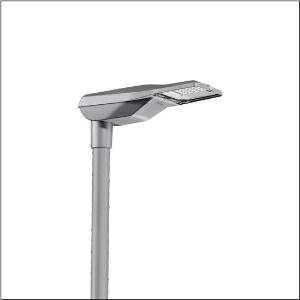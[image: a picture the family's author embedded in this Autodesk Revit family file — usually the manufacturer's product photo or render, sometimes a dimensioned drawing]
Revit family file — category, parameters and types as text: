
# Revit family: streetlight_sl_21_micro___stw1_0a_5xe5e63a08cb_6596
name_source: partatom
category: Lighting Fixtures
units: mm (PartAtom-declared; Revit-internal decimal feet)

## family parameters
Cut with Voids When Loaded = No
Host = Face
Light Source = No
Part Type = Normal
Room Calculation Point = No
Round Connector Dimension = Use Diameter
Shared = No

## types (1)
- --- (1 x LED, 2050 lm, 15.8 W, 2700K)
    Apparent Load = 16 VA
    CIE Flux Codes = 38 75 98 100 100
    Color Rendering = 70
    Color Temperature = 2700K
    Default Elevation = 1800 mm
    Description = Streetlight SL 21 micro, mast luminaire, primary light control with lens, of PMMA, primary optical cover: cover, of toughened safety glass, transparent, light distribution: STW1.0a, light emission: direct distribution, primary light characteristic: asymmetric, installation type: side-entry, post-top, LED, 3G 1.5mm², High Power LED, rated luminous flux: 2.050lm, luminous efficacy: 130lm/W, light colour: 727, colour temperature: 2700K, control: flexible luminous flux parameterisation, time-dependent luminous flux control, constant luminous flux control, overheat protection, mains connection: 230..240V, AC, 50/60Hz, connection cable pre-assembled, cable length: 5,5m, wiring characteristics: H07RN-F, start of lifetime: 16W, end of service life: 16W, reduction: 8W, luminaire housing, of diecast aluminium, powder-coated, Siteco® metallic grey (DB 702S), corrosivity category C5 mid according to DIN EN ISO 12944, please order mast flange separately, inclination adjustable: 0°, 5°, 10°, 15°, sealing non-destructively replaceable, multi-level sealing system, length: 528mm, width: 235mm, height: 110mm, mast flange for spigot size: 42mm (side-entry): 5XC10008XM4, 60/48mm (side-entry/post-top): 5XC10108XM2, 76/60mm (side-entry/post-top): 5XC10108XM1, protection rating (complete): IP66, insulation class (complete): insulation class II (safety insulation), certification: CE, ENEC, ENEC+, VDE, impact resistance: IK09, permissible operating ambient temperature for outdoor applications: -40..+50°C, standard-compliant lighting for roads and squares, packaging unit: 1 piece

Light Distribution: STW1.0a
    Height = 110 mm
    Lamp = 1 x LED
    Lamp Light Flux = 2050 lm
    Lamp Power = 15.8 W
    Lamp count = 1
    Length = 528 mm
    Luminous efficacy = 130 lm/W
    Manufacturer = Siteco
    ModVariant = No
    Model = 5XE5E63A08CB
    Number of Poles = 1
    OnlyDefault = Yes
    Power Factor = 1
    Product Name = Streetlight SL 21 micro | STW1.0a
    Product group = mast luminaire | pylon top
    ProductGroupID = 6100
    Protection Class = Protection class II
    Protection Degree = IP 66
    RLX_Detail_Level = 1
    RLX_Emergency_Light_Flux = 0 lm
    RLX_Emergency_Type = 0
    RLX_Emergency_Type_DB = No
    RlxData = <blob elided: 97817 chars, md5=e940a29d>
    Socket = socket
    Standby Power = 0 W
    System Light Flux = 2050 lm
    System Power = 16 W
    Type Comments = factory setting: luminous flux: 100 % | Output Level: 100 % | 300 mA
    Type Image = l_1006881.jpg
    URL = http://relux.com
    VarID = @adj_105205
    Voltage = 0 V
    Weight = 0.00 kg
    Width = 235 mm

## geometry (parser evidence)
native form markers: Blend x4, Sweep x11
no freeform markers — native parametric forms only
